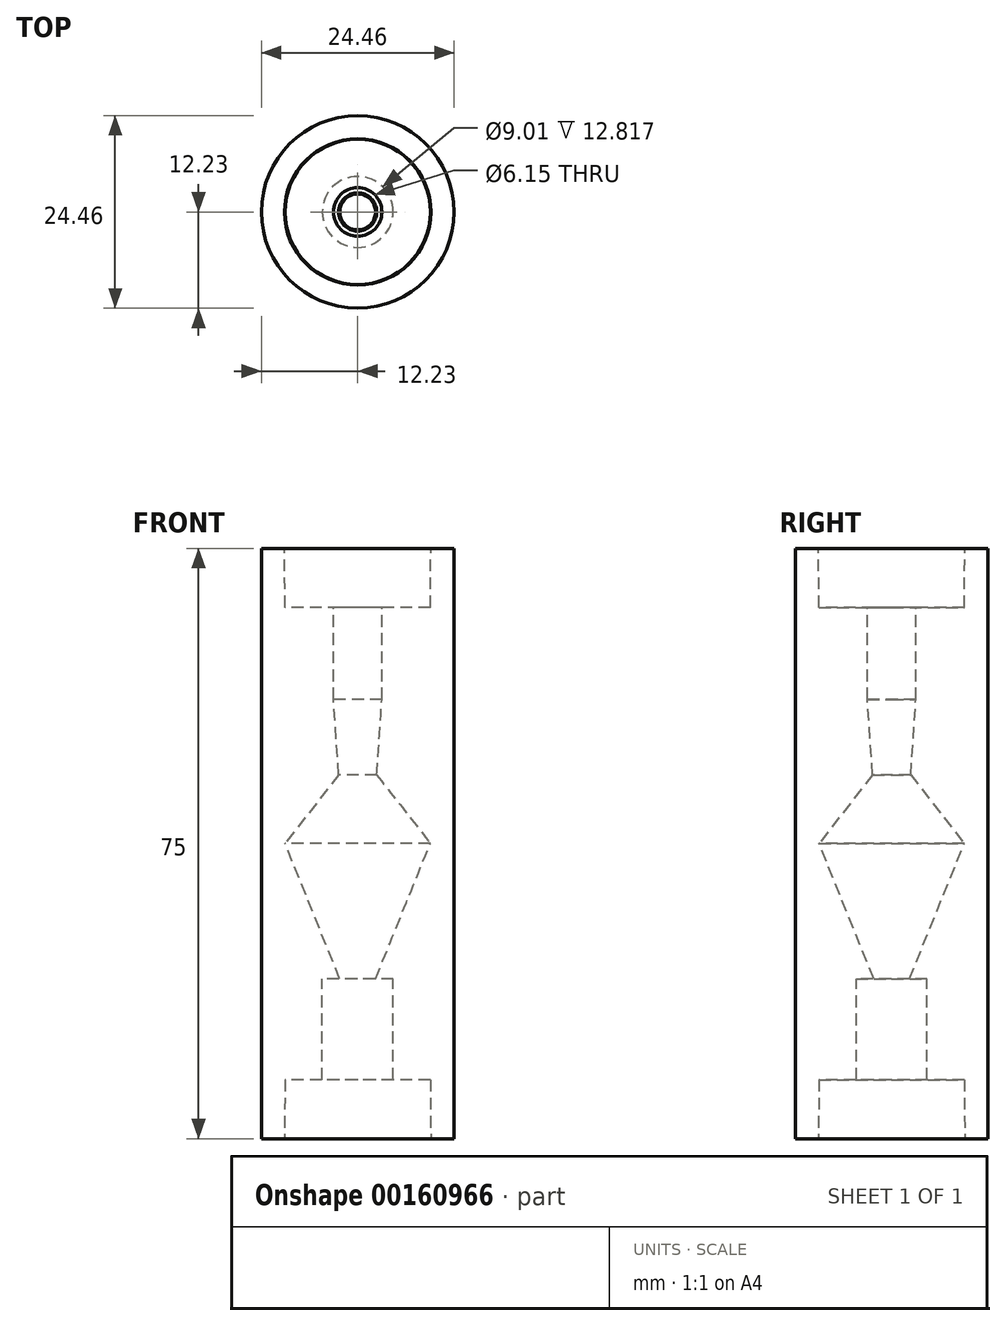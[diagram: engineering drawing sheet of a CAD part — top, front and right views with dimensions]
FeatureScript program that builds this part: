
annotation { "Feature Type Name" : "Feature", "Feature Type Description" : "" }
export const myFeature = defineFeature(function(context is Context, id is Id, definition is map)
    precondition{}
    {
        {
            var Q0;
            Q0=qCreatedBy(makeId("Front.planeOp"),FACE);
            var sketch = newSketch(context, id + "F0", { "sketchPlane" : qUnion([Q0])});
            skLineSegment(sketch, "E0.bottom", {"start": v(12.22, 30) * mm, "end": v(-12.23, 30) * mm});
            skLineSegment(sketch, "E0.top", {"start": v(12.22, -30) * mm, "end": v(-12.23, -30) * mm});
            skLineSegment(sketch, "E0.left", {"start": v(12.23, 30) * mm, "end": v(12.22, -30) * mm});
            skLineSegment(sketch, "E0.right", {"start": v(-12.22, 30) * mm, "end": v(-12.23, -30) * mm});
            skPoint(sketch, "E0.middle", {"position": v(0, 0) * mm});
            skLineSegment(sketch, "E1", {"start": v(-9.23, 30) * mm, "end": v(-9.23, -30) * mm});
            skLineSegment(sketch, "E2", {"start": v(9.22, -30) * mm, "end": v(9.23, 30) * mm});
            skLineSegment(sketch, "E3", {"start": v(-3.07, 18.3) * mm, "end": v(-3.07, 30) * mm});
            skLineSegment(sketch, "E4.MirrorCS", {"start": v(3.07, 18.3) * mm, "end": v(3.07, 30) * mm});
            skLineSegment(sketch, "E5", {"start": v(3.07, 18.3) * mm, "end": v(2.43, 8.71) * mm});
            skLineSegment(sketch, "E6", {"start": v(2.43, 8.71) * mm, "end": v(9.23, 0) * mm});
            skLineSegment(sketch, "E7.MirrorCS", {"start": v(-3.07, 18.3) * mm, "end": v(-2.43, 8.71) * mm});
            skLineSegment(sketch, "E8.MirrorCS", {"start": v(-2.43, 8.71) * mm, "end": v(-9.22, 0) * mm});
            skLineSegment(sketch, "E9", {"start": v(-9.22, 0) * mm, "end": v(-4.5, -17.18) * mm});
            skLineSegment(sketch, "E10", {"start": v(-4.5, -17.18) * mm, "end": v(-4.5, -30) * mm});
            skLineSegment(sketch, "E11", {"start": v(-4.5, -17.18) * mm, "end": v(-2.28, -17.18) * mm});
            skLineSegment(sketch, "E12", {"start": v(-2.28, -17.18) * mm, "end": v(-9.23, 0) * mm});
            skLineSegment(sketch, "E13.MirrorCS", {"start": v(2.27, -17.18) * mm, "end": v(9.22, 0) * mm});
            skLineSegment(sketch, "E14.MirrorCS", {"start": v(9.23, 0) * mm, "end": v(4.5, -17.18) * mm});
            skLineSegment(sketch, "E15.MirrorCS", {"start": v(4.5, -17.18) * mm, "end": v(2.28, -17.18) * mm});
            skLineSegment(sketch, "E16.MirrorCS", {"start": v(4.5, -17.18) * mm, "end": v(4.5, -30) * mm});
            skLineSegment(sketch, "E17", {"start": v(0, 30) * mm, "end": v(0, -30) * mm});
            skLineSegment(sketch, "E18", {"start": v(-12.22, 30) * mm, "end": v(-12.22, 37.5) * mm});
            skLineSegment(sketch, "E19", {"start": v(-12.22, 37.5) * mm, "end": v(-9.3, 37.5) * mm});
            skLineSegment(sketch, "E20", {"start": v(-9.3, 37.5) * mm, "end": v(-9.23, 30) * mm});
            skLineSegment(sketch, "E21.MirrorCS", {"start": v(-12.22, -37.5) * mm, "end": v(-9.3, -37.5) * mm});
            skLineSegment(sketch, "E22.MirrorCS", {"start": v(-9.3, -37.5) * mm, "end": v(-9.23, -30) * mm});
            skLineSegment(sketch, "E23.MirrorCS", {"start": v(-12.23, -30) * mm, "end": v(-12.23, -37.5) * mm});
            skSolve(sketch);
        }
        {
            var Q0;
            {var subQ4=sQuery(id+"F0.wireOp",EDGE,"E0.right");Q0=makeQuery(id+"F0.imprint","IMPRINT",FACE,{"disambiguationData":[TD([[makeQuery(id+"F0.imprint","IMPRINT",EDGE,{"derivedFrom":subQ4}),1.0]])]});}
            var Q1;
            {var subQ4=sQuery(id+"F0.wireOp",EDGE,"E9");Q1=makeQuery(id+"F0.imprint","IMPRINT",FACE,{"disambiguationData":[TD([[makeQuery(id+"F0.imprint","IMPRINT",EDGE,{"derivedFrom":subQ4}),-1.0]])]});}
            var Q2;
            Q2=makeQuery(id+"F0.imprint","IMPRINT",FACE,{"disambiguationData":[TD([[makeQuery(id+"F0.imprint","IMPRINT",EDGE,{"derivedFrom":sQuery(id+"F0.wireOp",EDGE,"E9")}),1.0]])]});
            var Q3;
            {var subQ0=sQuery(id+"F0.wireOp",EDGE,"E3");Q3=makeQuery(id+"F0.imprint","IMPRINT",FACE,{"disambiguationData":[TD([[makeQuery(id+"F0.imprint","IMPRINT",EDGE,{"derivedFrom":subQ0}),1.0]])]});}
            var Q4;
            {var subQ0=sQuery(id+"F0.wireOp",EDGE,"E18");Q4=makeQuery(id+"F0.imprint","IMPRINT",FACE,{"disambiguationData":[TD([[makeQuery(id+"F0.imprint","IMPRINT",EDGE,{"derivedFrom":subQ0}),-1.0]])]});}
            var Q5;
            Q5=makeQuery(id+"F0.imprint","IMPRINT",FACE,{"disambiguationData":[TD([[makeQuery(id+"F0.imprint","IMPRINT",EDGE,{"derivedFrom":sQuery(id+"F0.wireOp",EDGE,"E21.MirrorCS")}),1.0]])]});
            var Q6;
            Q6=sQuery(id+"F0.wireOp",EDGE,"E17");
            revolve(context, id + "F1", {"entities" : qUnion([Q0, Q1, Q2, Q3, Q4, Q5]), "axis" : qUnion([Q6]), "revolveType" : RevolveType.FULL});
        }
    });
